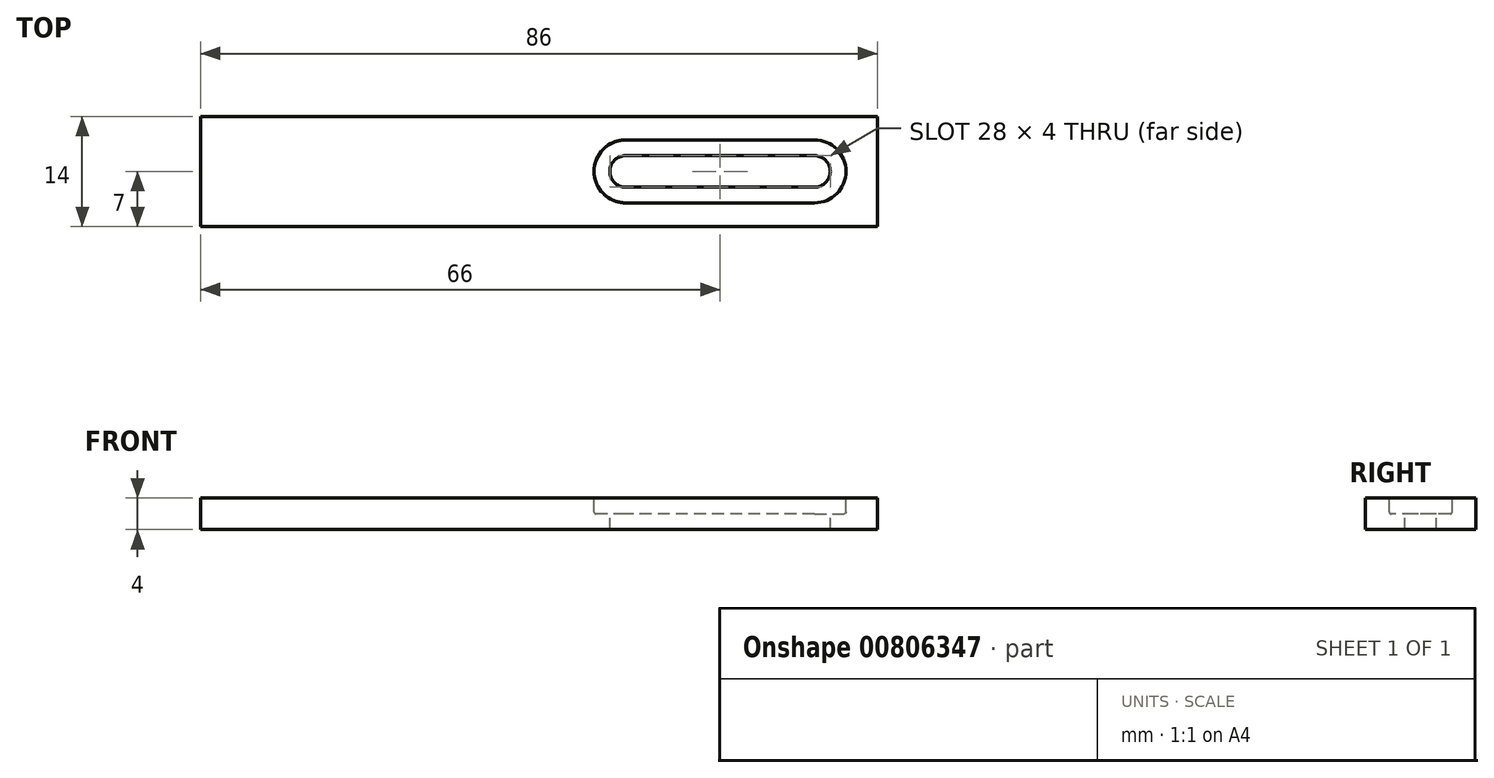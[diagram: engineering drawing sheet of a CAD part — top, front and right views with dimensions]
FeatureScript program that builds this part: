
annotation { "Feature Type Name" : "Feature", "Feature Type Description" : "" }
export const myFeature = defineFeature(function(context is Context, id is Id, definition is map)
    precondition{}
    {
        {
            var Q0;
            Q0=qCreatedBy(makeId("Top.planeOp"),FACE);
            var sketch = newSketch(context, id + "F0", { "sketchPlane" : qUnion([Q0])});
            skLineSegment(sketch, "E0.bottom", {"start": v(43, -7) * mm, "end": v(-43, -7) * mm});
            skLineSegment(sketch, "E0.top", {"start": v(43, 7) * mm, "end": v(-43, 7) * mm});
            skLineSegment(sketch, "E0.left", {"start": v(43, -7) * mm, "end": v(43, 7) * mm});
            skLineSegment(sketch, "E0.right", {"start": v(-43, -7) * mm, "end": v(-43, 7) * mm});
            skPoint(sketch, "E0.middle", {"position": v(0, 0) * mm});
            skSolve(sketch);
        }
        {
            var Q0;
            Q0 = qSketchRegion(id + "F0", true);
            extrude(context, id + "F1", {"entities" : qUnion([Q0]), "depth" : 4 * mm, "offsetDistance" : 25.4 * mm});
        }
        {
            var Q0;
            Q0=makeQuery(id+"F1.opExtrude","CAP_FACE",FACE,{"disambiguationData":[OSD([sQuery(id+"F0.wireOp",EDGE,"E0.bottom"),sQuery(id+"F0.wireOp",EDGE,"E0.top"),sQuery(id+"F0.wireOp",EDGE,"E0.left"),sQuery(id+"F0.wireOp",EDGE,"E0.right")])],"isStart":false});
            var sketch = newSketch(context, id + "F2", { "sketchPlane" : qUnion([Q0])});
            skLineSegment(sketch, "E1", {"start": v(-43, 0) * mm, "end": v(43, 0) * mm, "construction": true});
            skCircle(sketch, "E2", {"center": v(35, 0) * mm, "radius": 2 * mm});
            skCircle(sketch, "E3", {"center": v(11, 0) * mm, "radius": 2 * mm});
            skLineSegment(sketch, "E4.bottom", {"start": v(11, -2) * mm, "end": v(35, -2) * mm});
            skLineSegment(sketch, "E4.top", {"start": v(11, 2) * mm, "end": v(35, 2) * mm});
            skLineSegment(sketch, "E4.left", {"start": v(11, -2) * mm, "end": v(11, 2) * mm});
            skLineSegment(sketch, "E4.right", {"start": v(35, -2) * mm, "end": v(35, 2) * mm});
            skSolve(sketch);
        }
        {
            var Q0;
            Q0 = qSketchRegion(id + "F2", true);
            extrude(context, id + "F3", {"entities" : qUnion([Q0]), "operationType" : NewBodyOperationType.REMOVE, "oppositeDirection" : true, "depth" : 4 * mm, "offsetDistance" : 25.4 * mm});
        }
        {
            var Q0;
            Q0=makeQuery(id+"F1.opExtrude","CAP_FACE",FACE,{"disambiguationData":[OSD([sQuery(id+"F0.wireOp",EDGE,"E0.bottom"),sQuery(id+"F0.wireOp",EDGE,"E0.top"),sQuery(id+"F0.wireOp",EDGE,"E0.left"),sQuery(id+"F0.wireOp",EDGE,"E0.right")])],"isStart":false});
            var sketch = newSketch(context, id + "F4", { "sketchPlane" : qUnion([Q0])});
            skLineSegment(sketch, "E5", {"start": v(-43, 0) * mm, "end": v(43, 0) * mm, "construction": true});
            skCircle(sketch, "E6", {"center": v(35, 0) * mm, "radius": 4 * mm});
            skCircle(sketch, "E7", {"center": v(11, 0) * mm, "radius": 4 * mm});
            skLineSegment(sketch, "E8.bottom", {"start": v(11, -4) * mm, "end": v(35, -4) * mm});
            skLineSegment(sketch, "E8.top", {"start": v(11, 4) * mm, "end": v(35, 4) * mm});
            skLineSegment(sketch, "E8.left", {"start": v(11, -4) * mm, "end": v(11, 4) * mm});
            skLineSegment(sketch, "E8.right", {"start": v(35, -4) * mm, "end": v(35, 4) * mm});
            skSolve(sketch);
        }
        {
            var Q0;
            Q0 = qSketchRegion(id + "F4", true);
            extrude(context, id + "F5", {"entities" : qUnion([Q0]), "operationType" : NewBodyOperationType.REMOVE, "oppositeDirection" : true, "depth" : 2 * mm, "offsetDistance" : 25.4 * mm});
        }
        {
            var Q0;
            Q0=makeQuery(id+"F5.boolean.opBoolean","COPY",EDGE,{"derivedFrom":makeQuery(id+"F5.opExtrude","CAP_EDGE",EDGE,{"disambiguationData":[OSD([sQuery(id+"F4.wireOp",EDGE,"E8.top")])],"isStart":false})});
            var Q1;
            Q1=makeQuery(id+"F5.boolean.opBoolean","COPY",EDGE,{"derivedFrom":makeQuery(id+"F5.opExtrude","CAP_EDGE",EDGE,{"disambiguationData":[OSD([sQuery(id+"F4.wireOp",EDGE,"E7")])],"isStart":false})});
            var Q2;
            Q2=makeQuery(id+"F5.boolean.opBoolean","COPY",EDGE,{"derivedFrom":makeQuery(id+"F5.opExtrude","CAP_EDGE",EDGE,{"disambiguationData":[OSD([sQuery(id+"F4.wireOp",EDGE,"E8.bottom")])],"isStart":false})});
            var Q3;
            Q3=makeQuery(id+"F5.boolean.opBoolean","COPY",EDGE,{"derivedFrom":makeQuery(id+"F5.opExtrude","CAP_EDGE",EDGE,{"disambiguationData":[OSD([sQuery(id+"F4.wireOp",EDGE,"E6")])],"isStart":false})});
            var Q4;
            Q4=makeQuery(id+"F5.boolean.opBoolean","COPY",EDGE,{"derivedFrom":makeQuery(id+"F5.opExtrude","CAP_EDGE",EDGE,{"disambiguationData":[OSD([sQuery(id+"F4.wireOp",EDGE,"E8.bottom")])],"isStart":true})});
            var Q5;
            Q5=makeQuery(id+"F5.boolean.opBoolean","COPY",EDGE,{"derivedFrom":makeQuery(id+"F5.opExtrude","CAP_EDGE",EDGE,{"disambiguationData":[OSD([sQuery(id+"F4.wireOp",EDGE,"E7")])],"isStart":true})});
            var Q6;
            Q6=makeQuery(id+"F5.boolean.opBoolean","COPY",EDGE,{"derivedFrom":makeQuery(id+"F5.opExtrude","CAP_EDGE",EDGE,{"disambiguationData":[OSD([sQuery(id+"F4.wireOp",EDGE,"E8.top")])],"isStart":true})});
            var Q7;
            Q7=makeQuery(id+"F5.boolean.opBoolean","COPY",EDGE,{"derivedFrom":makeQuery(id+"F5.opExtrude","CAP_EDGE",EDGE,{"disambiguationData":[OSD([sQuery(id+"F4.wireOp",EDGE,"E6")])],"isStart":true})});
            fillet(context, id + "F6", {"entities" : qUnion([Q0, Q1, Q2, Q3, Q4, Q5, Q6, Q7]), "radius" : 0.25 * mm, "tangentPropagation" : true, "allowEdgeOverflow" : false});
        }
    });
